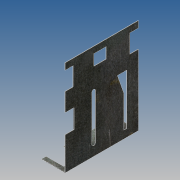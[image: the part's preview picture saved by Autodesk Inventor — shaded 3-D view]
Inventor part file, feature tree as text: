
AUTODESK INVENTOR PART (.ipt)
format: ipt  version: 2016 (Build 200138000, 138)  size: 166,912 bytes
history: native  units: mm
features: extrude x4, sketch x4
ambient origin geometry x8: Origin, YZ Plane, XZ Plane, XY Plane, X Axis, Y Axis, Z Axis, Center Point
bodies: Solid1 (feature_tree)
feature tree (8):
  extrude  "Extrusion1"  Depth=130.0mm
  extrude  "Extrusion2"  Depth=100.0mm TaperAngle=0.0deg
  extrude  "Extrusion3"  Depth=1.75mm
  extrude  "Extrusion4"  Depth=100.0mm
  sketch  "Sketch1"  dims[d0=0.5mm d1=130.0mm]
  sketch  "Sketch2"  dims[d2=32.0mm d3=100.0mm d4=0.0mm]
  sketch  "Sketch3"  dims[d5=100.0mm d6=0.0mm d7=1.75mm]
  sketch  "Sketch4"  dims[d8=15.0mm d9=20.0mm d10=15.0mm d11=5.0mm d12=100.0mm d13=0.0mm d14=100.0mm d15=0.0mm]
